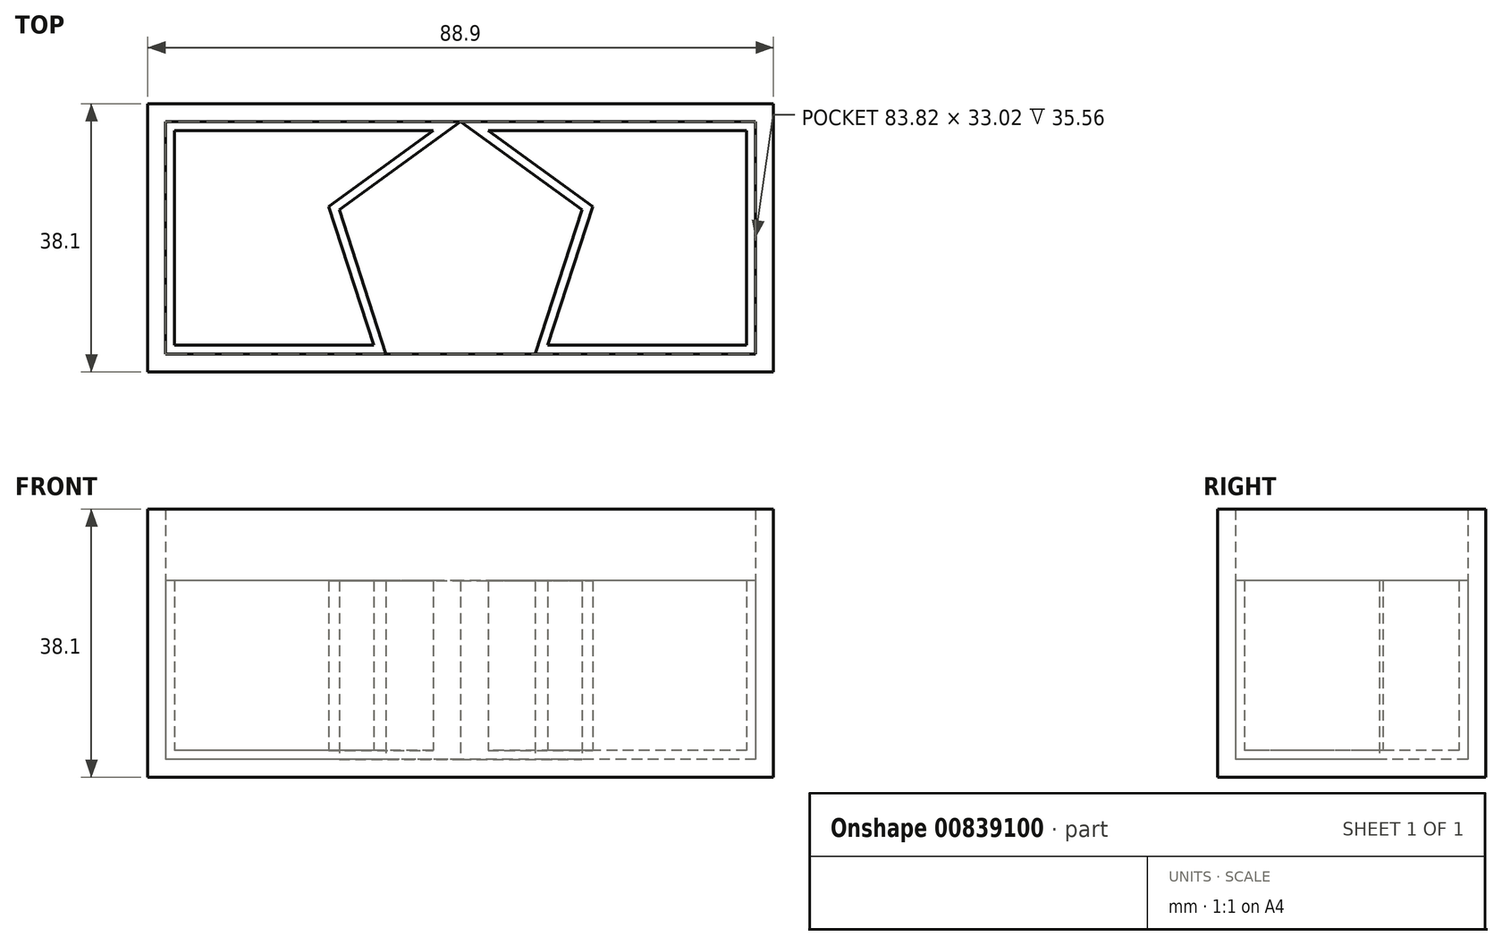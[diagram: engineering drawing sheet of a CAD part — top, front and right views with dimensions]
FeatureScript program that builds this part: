
annotation { "Feature Type Name" : "Feature", "Feature Type Description" : "" }
export const myFeature = defineFeature(function(context is Context, id is Id, definition is map)
    precondition{}
    {
        {
            var Q0;
            Q0=qCreatedBy(makeId("Top.planeOp"),FACE);
            var sketch = newSketch(context, id + "F0", { "sketchPlane" : qUnion([Q0])});
            skPoint(sketch, "E0.middle", {"position": v(0, 0) * mm});
            skLineSegment(sketch, "E1.bottom", {"start": v(44.45, 19.05) * mm, "end": v(-44.45, 19.05) * mm});
            skLineSegment(sketch, "E1.top", {"start": v(44.45, -19.05) * mm, "end": v(-44.45, -19.05) * mm});
            skLineSegment(sketch, "E1.left", {"start": v(44.45, 19.05) * mm, "end": v(44.45, -19.05) * mm});
            skLineSegment(sketch, "E1.right", {"start": v(-44.45, 19.05) * mm, "end": v(-44.45, -19.05) * mm});
            skSolve(sketch);
        }
        {
            var Q0;
            Q0=makeQuery(id+"F0.imprint","IMPRINT",FACE,{"disambiguationData":[TD([[makeQuery(id+"F0.imprint","IMPRINT",EDGE,{"derivedFrom":sQuery(id+"F0.wireOp",EDGE,"E1.bottom")}),1.0]])]});
            extrude(context, id + "F1", {"entities" : qUnion([Q0]), "depth" : 38.1 * mm, "offsetDistance" : 25.4 * mm});
        }
        {
            var Q0;
            Q0=makeQuery(id+"F1.opExtrude","CAP_FACE",FACE,{"disambiguationData":[OSD([sQuery(id+"F0.wireOp",EDGE,"E1.bottom"),sQuery(id+"F0.wireOp",EDGE,"E1.top"),sQuery(id+"F0.wireOp",EDGE,"E1.left"),sQuery(id+"F0.wireOp",EDGE,"E1.right")])],"isStart":false});
            shell(context, id + "F2", {"entities" : qUnion([Q0]), "thickness" : 2.54 * mm});
        }
        {
            var Q0;
            Q0=makeQuery(id+"F2.opShell","OFFSET_FACE",FACE,{"disambiguationData":[OSD([sQuery(id+"F0.wireOp",EDGE,"E1.bottom"),sQuery(id+"F0.wireOp",EDGE,"E1.top"),sQuery(id+"F0.wireOp",EDGE,"E1.left"),sQuery(id+"F0.wireOp",EDGE,"E1.right")])]});
            var sketch = newSketch(context, id + "F3", { "sketchPlane" : qUnion([Q0])});
            skLineSegment(sketch, "E2.0", {"start": v(0, 16.51) * mm, "end": v(15.7, 5.1) * mm});
            skLineSegment(sketch, "E2.4", {"start": v(-15.7, 5.1) * mm, "end": v(0, 16.51) * mm});
            skLineSegment(sketch, "E3.0", {"start": v(0, 16.51) * mm, "end": v(16.68, 4.4) * mm});
            skLineSegment(sketch, "E3.4", {"start": v(-16.68, 4.4) * mm, "end": v(0, 16.51) * mm});
            skLineSegment(sketch, "E4.0", {"start": v(0, 16.51) * mm, "end": v(17.25, 3.98) * mm});
            skLineSegment(sketch, "E4.4", {"start": v(-17.25, 3.98) * mm, "end": v(0, 16.51) * mm});
            skLineSegment(sketch, "E5", {"start": v(-17.25, 3.98) * mm, "end": v(-10.6, -16.5) * mm});
            skLineSegment(sketch, "E6.MirrorCS", {"start": v(17.25, 3.98) * mm, "end": v(10.6, -16.51) * mm});
            skLineSegment(sketch, "E7", {"start": v(-10.6, -16.5) * mm, "end": v(10.6, -16.5) * mm});
            skSolve(sketch);
        }
        {
            var Q0;
            {var subQ0=sQuery(id+"F3.wireOp",EDGE,"E5");Q0=makeQuery(id+"F3.imprint","IMPRINT",FACE,{"disambiguationData":[TD([[makeQuery(id+"F3.imprint","IMPRINT",EDGE,{"derivedFrom":subQ0}),-1.0]])]});}
            var Q1;
            {var subQ0=sQuery(id+"F3.wireOp",EDGE,"E6.MirrorCS");Q1=makeQuery(id+"F3.imprint","IMPRINT",FACE,{"disambiguationData":[TD([[makeQuery(id+"F3.imprint","IMPRINT",EDGE,{"derivedFrom":subQ0}),1.0]])]});}
            extrude(context, id + "F4", {"entities" : qUnion([Q0, Q1]), "depth" : 25.4 * mm, "offsetDistance" : 25.4 * mm});
        }
        {
            var Q0;
            Q0=makeQuery(id+"F4.opExtrude","CAP_FACE",FACE,{"disambiguationData":[OSD([sQuery(id+"F0.wireOp",EDGE,"E1.bottom"),sQuery(id+"F0.wireOp",EDGE,"E1.top"),sQuery(id+"F0.wireOp",EDGE,"E1.right"),sQuery(id+"F3.wireOp",EDGE,"E4.4"),sQuery(id+"F3.wireOp",EDGE,"E5")])],"isStart":false});
            shell(context, id + "F5", {"entities" : qUnion([Q0]), "thickness" : 1.27 * mm});
        }
        {
            var Q0;
            Q0=makeQuery(id+"F4.opExtrude","CAP_FACE",FACE,{"disambiguationData":[OSD([sQuery(id+"F0.wireOp",EDGE,"E1.bottom"),sQuery(id+"F0.wireOp",EDGE,"E1.top"),sQuery(id+"F0.wireOp",EDGE,"E1.left"),sQuery(id+"F3.wireOp",EDGE,"E4.0"),sQuery(id+"F3.wireOp",EDGE,"E6.MirrorCS")])],"isStart":false});
            shell(context, id + "F6", {"entities" : qUnion([Q0]), "thickness" : 1.27 * mm});
        }
    });
